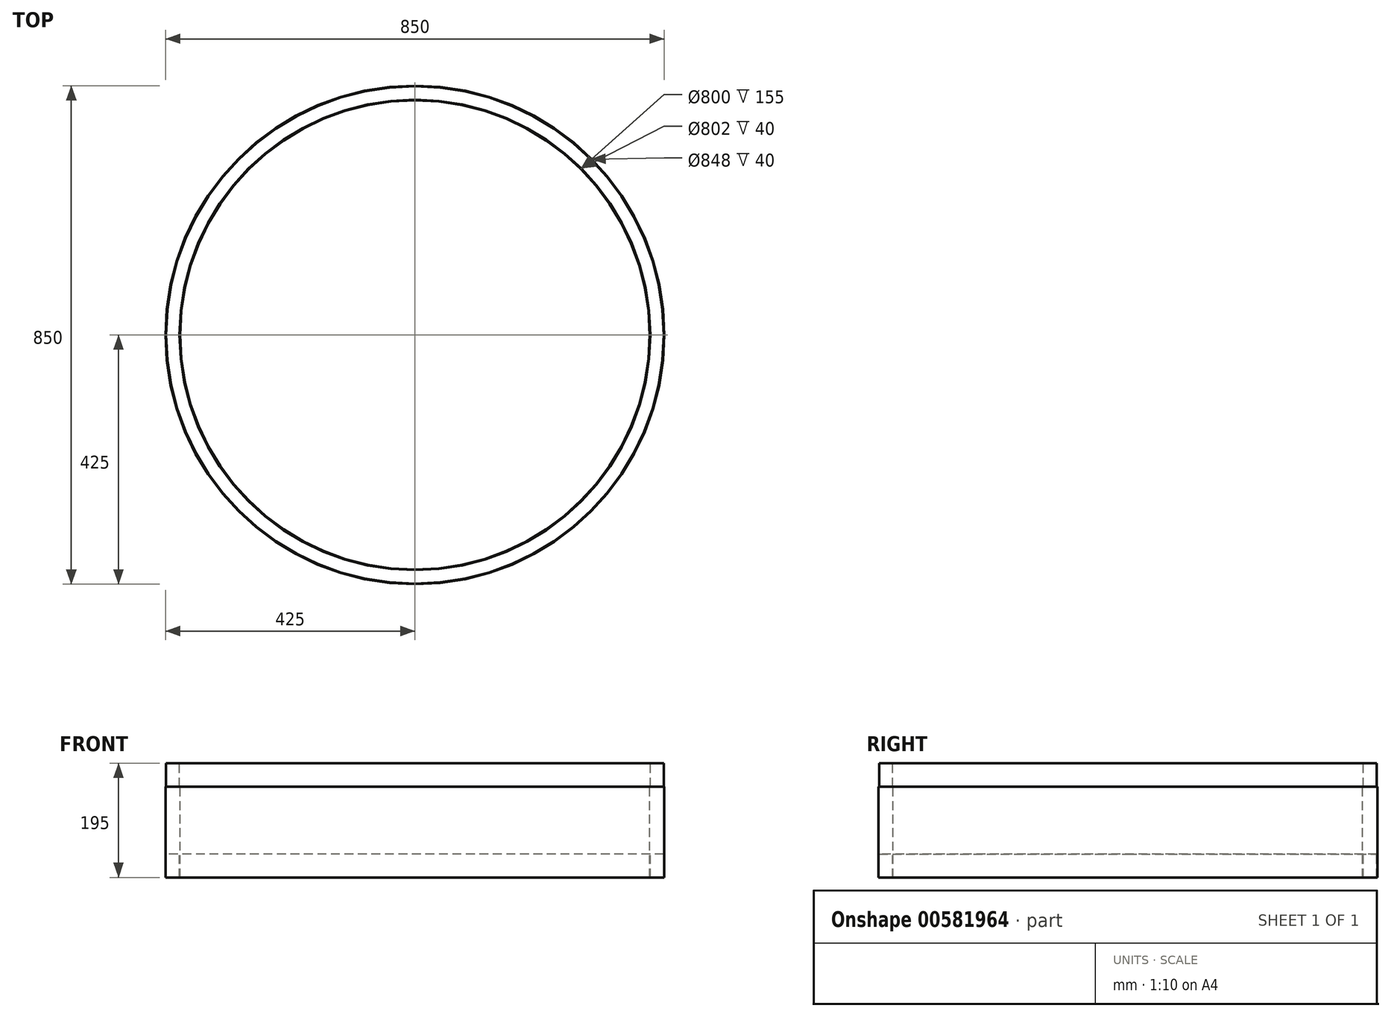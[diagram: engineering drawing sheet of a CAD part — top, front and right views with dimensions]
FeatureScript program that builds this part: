
annotation { "Feature Type Name" : "Feature", "Feature Type Description" : "" }
export const myFeature = defineFeature(function(context is Context, id is Id, definition is map)
    precondition{}
    {
        {
            var Q0;
            Q0=qCreatedBy(makeId("Front.planeOp"),FACE);
            var sketch = newSketch(context, id + "F0", { "sketchPlane" : qUnion([Q0])});
            skLineSegment(sketch, "E0", {"start": v(0, 345.75) * mm, "end": v(0, -558.03) * mm, "construction": true});
            skLineSegment(sketch, "E1", {"start": v(-400, -518.84) * mm, "end": v(-400, -363.84) * mm});
            skLineSegment(sketch, "E2", {"start": v(-400, -363.84) * mm, "end": v(-401, -363.84) * mm});
            skLineSegment(sketch, "E3", {"start": v(-401, -363.84) * mm, "end": v(-401, -323.84) * mm});
            skLineSegment(sketch, "E4", {"start": v(-401, -323.84) * mm, "end": v(-424, -323.84) * mm});
            skLineSegment(sketch, "E5", {"start": v(-424, -323.84) * mm, "end": v(-424, -363.84) * mm});
            skLineSegment(sketch, "E6", {"start": v(-424, -363.84) * mm, "end": v(-425, -363.84) * mm});
            skLineSegment(sketch, "E7", {"start": v(-425, -363.84) * mm, "end": v(-425, -518.84) * mm});
            skLineSegment(sketch, "E8", {"start": v(-425, -518.84) * mm, "end": v(-424, -518.84) * mm});
            skLineSegment(sketch, "E9", {"start": v(-424, -518.84) * mm, "end": v(-424, -478.84) * mm});
            skLineSegment(sketch, "E10", {"start": v(-424, -478.84) * mm, "end": v(-401, -478.84) * mm});
            skLineSegment(sketch, "E11", {"start": v(-401, -478.84) * mm, "end": v(-401, -518.84) * mm});
            skLineSegment(sketch, "E12", {"start": v(-401, -518.84) * mm, "end": v(-400, -518.84) * mm});
            skSolve(sketch);
        }
        {
            var Q0;
            Q0=qSketchRegion(id+"F0",true);
            var Q1;
            Q1=sQuery(id+"F0.wireOp",EDGE,"E0");
            revolve(context, id + "F1", {"entities" : qUnion([Q0]), "axis" : qUnion([Q1]), "revolveType" : RevolveType.FULL});
        }
    });
